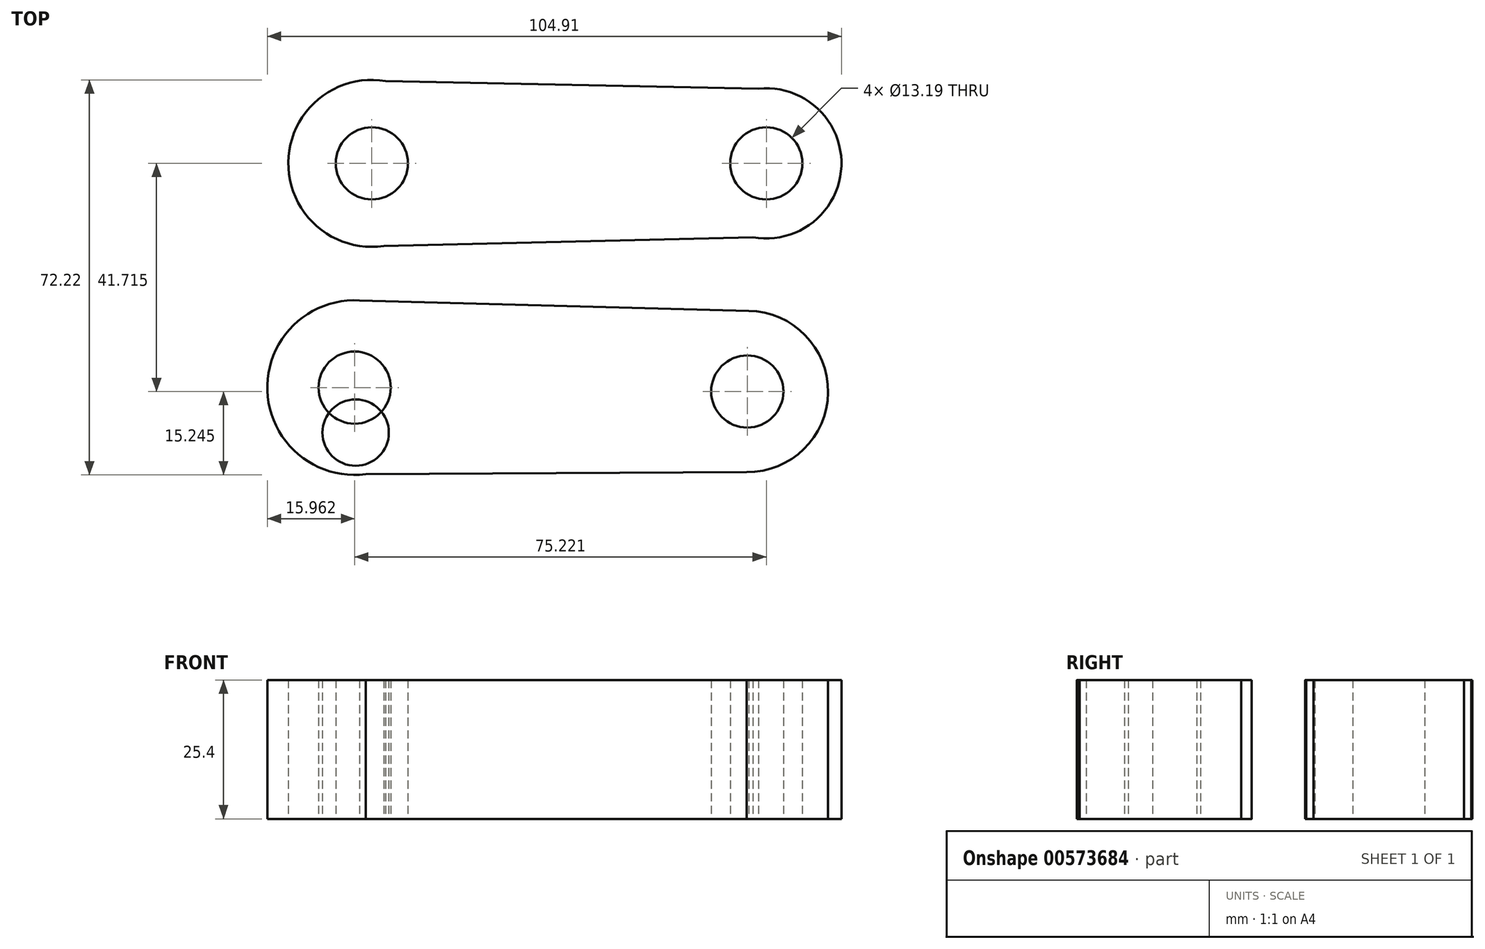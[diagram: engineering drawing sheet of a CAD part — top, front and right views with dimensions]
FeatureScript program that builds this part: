
annotation { "Feature Type Name" : "Feature", "Feature Type Description" : "" }
export const myFeature = defineFeature(function(context is Context, id is Id, definition is map)
    precondition{}
    {
        {
            var Q0;
            Q0=qCreatedBy(makeId("Top.planeOp"),FACE);
            var sketch = newSketch(context, id + "F0", { "sketchPlane" : qUnion([Q0])});
            skCircle(sketch, "E0", {"center": v(42.47, 0) * mm, "radius": 6.6 * mm});
            skCircle(sketch, "E1", {"center": v(-29.6, 0) * mm, "radius": 6.6 * mm});
            skCircle(sketch, "E2", {"center": v(-29.6, 0) * mm, "radius": 15.26 * mm});
            skCircle(sketch, "E3", {"center": v(42.47, 0) * mm, "radius": 13.73 * mm});
            skLineSegment(sketch, "E4", {"start": v(-27.44, -15.1) * mm, "end": v(40.03, -13.51) * mm});
            skLineSegment(sketch, "E5", {"start": v(-27.08, 15.05) * mm, "end": v(41.06, 13.66) * mm});
            skSolve(sketch);
        }
        {
            var Q0;
            Q0 = qSketchRegion(id + "F0", true);
            extrude(context, id + "F1", {"entities" : qUnion([Q0]), "depth" : 25.4 * mm, "offsetDistance" : 25.4 * mm});
        }
        {
            var Q0;
            Q0=qCreatedBy(makeId("Top.planeOp"),FACE);
            var sketch = newSketch(context, id + "F2", { "sketchPlane" : qUnion([Q0])});
            skCircle(sketch, "E6", {"center": v(-32.56, -49.23) * mm, "radius": 6.07 * mm});
            skSolve(sketch);
        }
        {
            var Q0;
            Q0 = qSketchRegion(id + "F2", true);
            extrude(context, id + "F3", {"entities" : qUnion([Q0]), "depth" : 25.4 * mm, "offsetDistance" : 25.4 * mm});
        }
        {
            var Q0;
            Q0=qCreatedBy(makeId("Top.planeOp"),FACE);
            var sketch = newSketch(context, id + "F4", { "sketchPlane" : qUnion([Q0])});
            skCircle(sketch, "E7", {"center": v(-32.75, -41) * mm, "radius": 6.6 * mm});
            skCircle(sketch, "E8", {"center": v(39, -41.71) * mm, "radius": 6.6 * mm});
            skCircle(sketch, "E9", {"center": v(-32.75, -41) * mm, "radius": 15.96 * mm});
            skCircle(sketch, "E10", {"center": v(39, -41.71) * mm, "radius": 14.75 * mm});
            skLineSegment(sketch, "E11", {"start": v(-34.62, -56.85) * mm, "end": v(39.28, -56.46) * mm});
            skLineSegment(sketch, "E12", {"start": v(-31.89, -25.07) * mm, "end": v(39.23, -26.96) * mm});
            skSolve(sketch);
        }
        {
            var Q0;
            Q0 = qSketchRegion(id + "F4", true);
            extrude(context, id + "F5", {"entities" : qUnion([Q0]), "depth" : 25.4 * mm, "offsetDistance" : 25.4 * mm});
        }
    });
